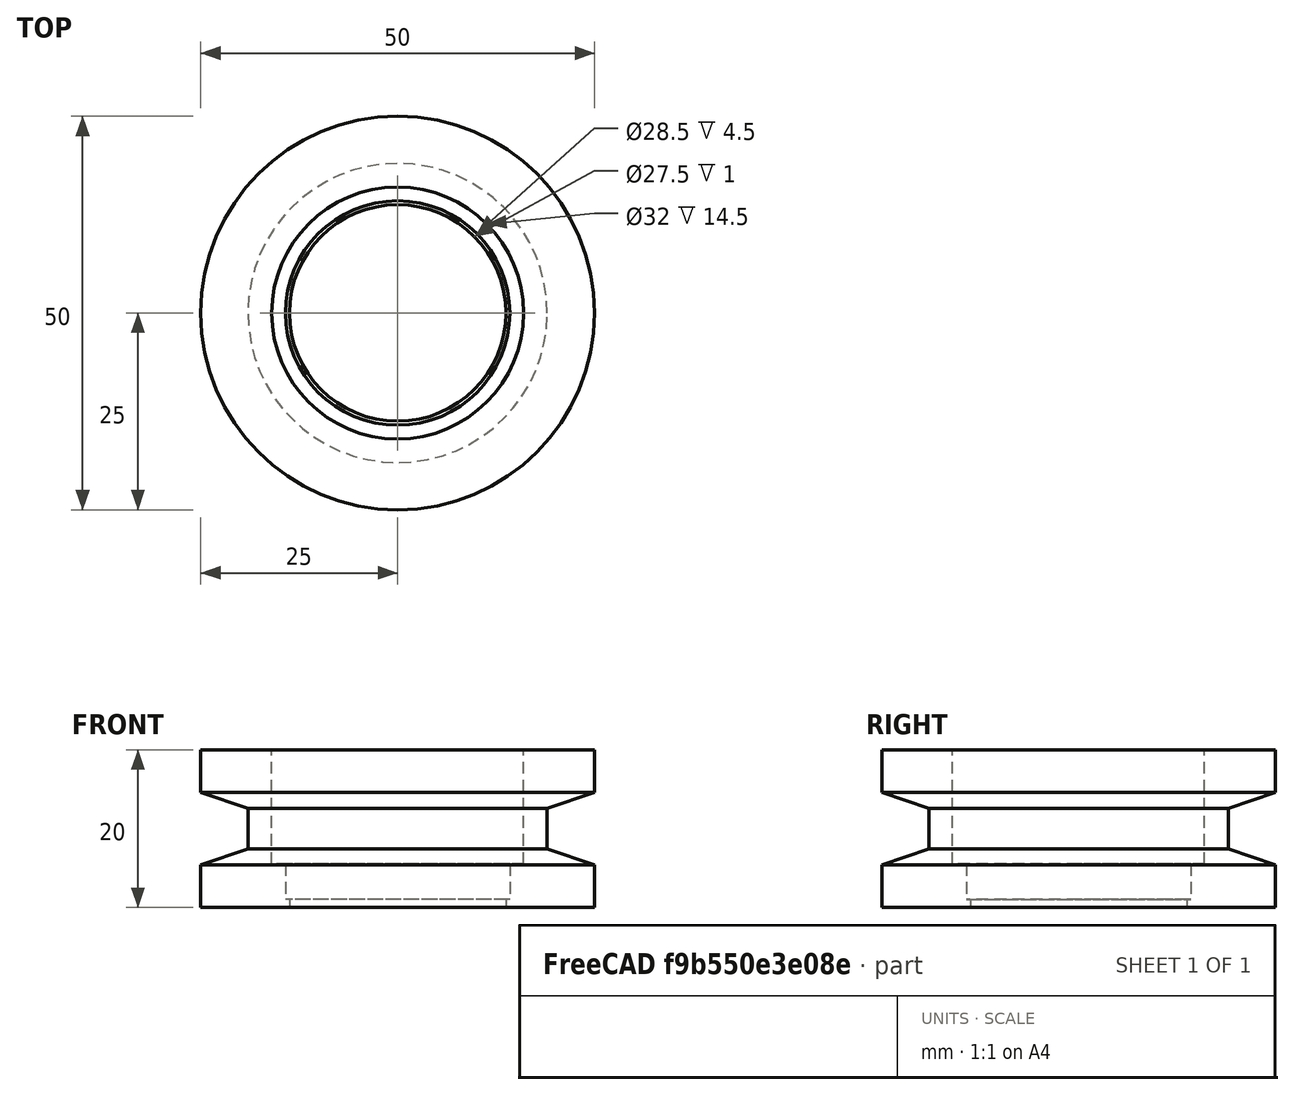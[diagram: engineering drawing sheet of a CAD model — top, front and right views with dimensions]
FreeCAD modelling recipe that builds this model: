
FCSTD DOCUMENT  (FreeCAD 0.15R4641 (Git))
Label: V_Belt_Pulley_V3
License: CC-BY 3.0
LicenseURL: http://creativecommons.org/licenses/by/3.0/
objects: Sketcher::SketchObject×1, PartDesign::Revolution×1, App::DocumentObjectGroup×1
note: 3 computed .brp shape members not serialized (recipe doc carries the construction recipe); baked Part::Feature solids carry a one-line shape summary decoded from their .brp

FEATURE [Sketcher::SketchObject] Sketch  label="1_BodyBase_Sketch"
  Placement = pos=(0,0,0) rot=(1,0,0;1.5708rad)
  sketch-geometry (12):
    g0: LineSegment StartX=13.75 StartY=-10 StartZ=0 EndX=25 EndY=-10 EndZ=0
    g1: LineSegment StartX=25 StartY=-10 StartZ=0 EndX=25 EndY=-4.61597 EndZ=0
    g2: LineSegment StartX=25 StartY=-4.61597 StartZ=0 EndX=19 EndY=-2.55 EndZ=0
    g3: LineSegment StartX=14.25 StartY=-4.5 StartZ=0 EndX=14.25 EndY=-9 EndZ=0
    g4: LineSegment StartX=14.25 StartY=-9 StartZ=0 EndX=13.75 EndY=-9 EndZ=0
    g5: LineSegment StartX=13.75 StartY=-9 StartZ=0 EndX=13.75 EndY=-10 EndZ=0
    g6: LineSegment StartX=19 StartY=2.55 StartZ=0 EndX=19 EndY=-2.55 EndZ=0
    g7: LineSegment StartX=14.25 StartY=-4.5 StartZ=0 EndX=16 EndY=-4.5 EndZ=0
    g8: LineSegment StartX=16 StartY=-4.5 StartZ=0 EndX=16 EndY=10 EndZ=0
    g9: LineSegment StartX=19 StartY=2.55 StartZ=0 EndX=25 EndY=4.61597 EndZ=0
    g10: LineSegment StartX=25 StartY=4.61597 StartZ=0 EndX=25 EndY=10 EndZ=0
    g11: LineSegment StartX=25 StartY=10 StartZ=0 EndX=16 EndY=10 EndZ=0
  constraints (35):
    c: Horizontal(g0)
    c: Coincident(g0,g1)
    c: Vertical(g1)
    c: Coincident(g1,g2)
    c: Coincident(g3,g4)
    c: Coincident(g4,g5)
    c: Coincident(g5,g0)
    c: Horizontal(g4)
    c: Vertical(g3)
    c: Vertical(g5)
    c: DistanceY(g5) = -1
    c: DistanceY(g3,g0) = -5.5
    c: DistanceX(g-1,g0) = 13.75
    c: DistanceX(g-1,g3) = 14.25
    c: Coincident(g6,g2)
    c: Vertical(g6)
    c: DistanceX(g-1,g0) = 25
    c: Coincident(g3,g7)
    c: Coincident(g7,g8)
    c: Vertical(g8)
    c: DistanceX(g-1,g8) = 16
    c: Horizontal(g7)
    c: Angle(g2,g0) = 0.331613
    c: DistanceX(g-1,g6) = 19
    c: Symmetric(g2,g6,g-1)
    c: Coincident(g6,g9)
    c: Coincident(g9,g10)
    c: Vertical(g10)
    c: Coincident(g10,g11)
    c: Horizontal(g11)
    c: Coincident(g8,g11)
    c: DistanceY(g6) = -5.1
    c: Symmetric(g1,g9,g-1)
    c: Symmetric(g10,g0,g-1)
    c: DistanceY(g10,g0) = -20
FEATURE [PartDesign::Revolution] Revolution001  label="1_BodyBase_Revolution"
  Angle = 360
  Axis = (0,0,1)
  Base = (0,0,0)
  Placement = pos=(0,0,0) rot=(1,0,0;1.5708rad)
  ReferenceAxis = -> Sketch [V_Axis]
  Reversed = true
  Sketch = -> Sketch
FEATURE [App::DocumentObjectGroup] Group  label="Body"
  Group = -> [Revolution001]
